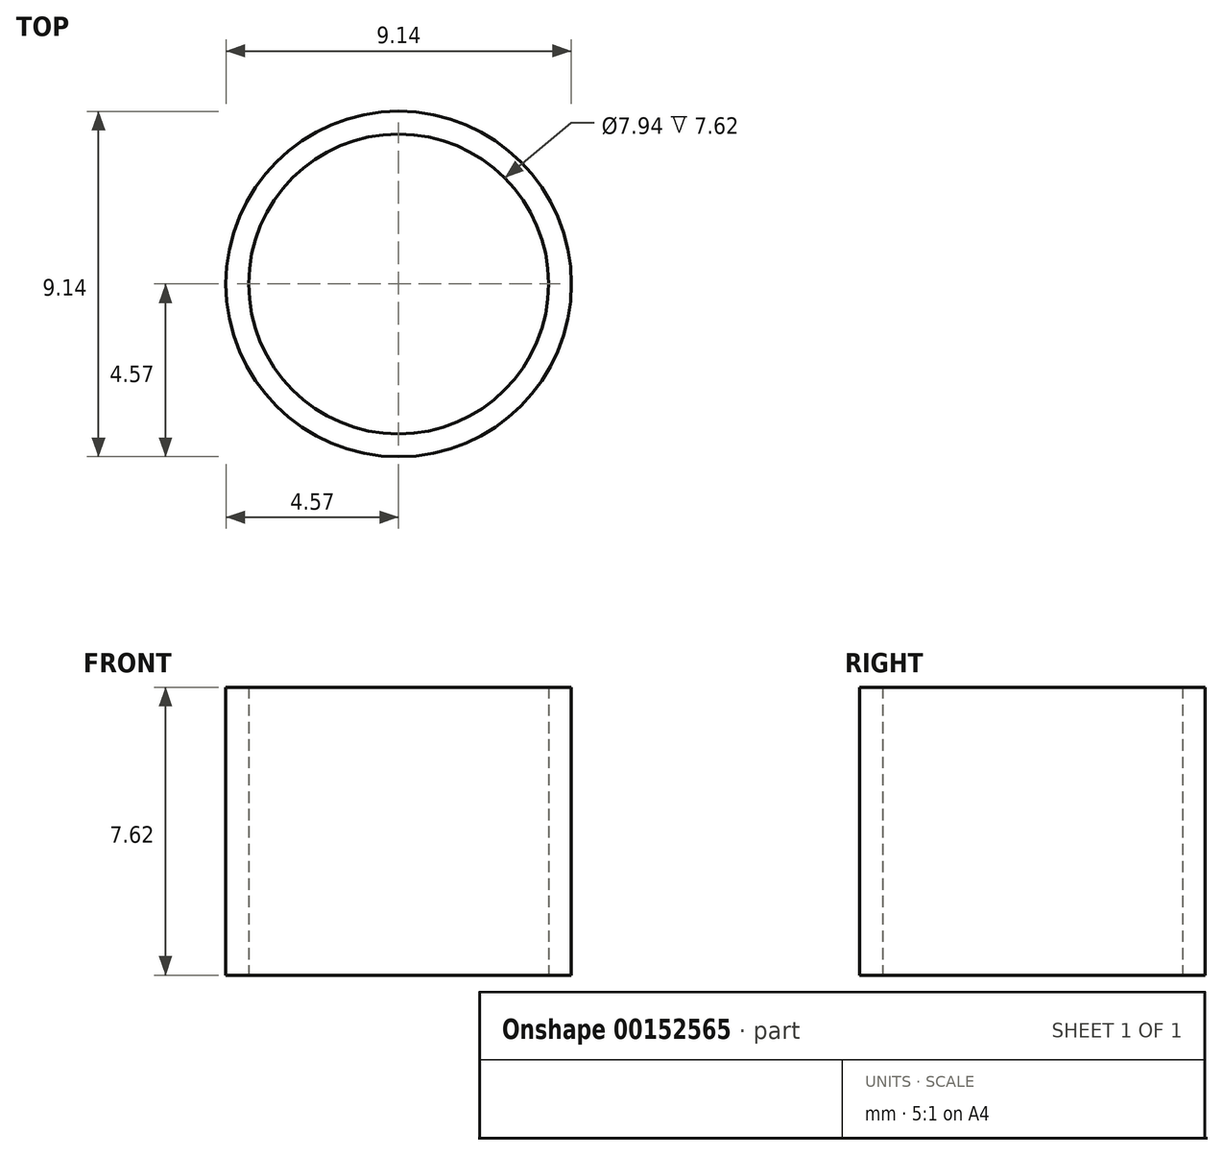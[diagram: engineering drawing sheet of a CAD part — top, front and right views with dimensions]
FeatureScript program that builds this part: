
annotation { "Feature Type Name" : "Feature", "Feature Type Description" : "" }
export const myFeature = defineFeature(function(context is Context, id is Id, definition is map)
    precondition{}
    {
        {
            var Q0;
            Q0=qCreatedBy(makeId("Top.planeOp"),FACE);
            var sketch = newSketch(context, id + "F0", { "sketchPlane" : qUnion([Q0])});
            skCircle(sketch, "E0", {"center": v(0, 0) * mm, "radius": 4.57 * mm});
            skCircle(sketch, "E1", {"center": v(0, 0) * mm, "radius": 3.97 * mm});
            skSolve(sketch);
        }
        {
            var Q0;
            Q0=makeQuery(id+"F0.imprint","IMPRINT",FACE,{"disambiguationData":[TD([[makeQuery(id+"F0.imprint","IMPRINT",EDGE,{"derivedFrom":sQuery(id+"F0.wireOp",EDGE,"E0")}),1.0]])]});
            extrude(context, id + "F1", {"entities" : qUnion([Q0]), "depth" : 7.62 * mm});
        }
    });
